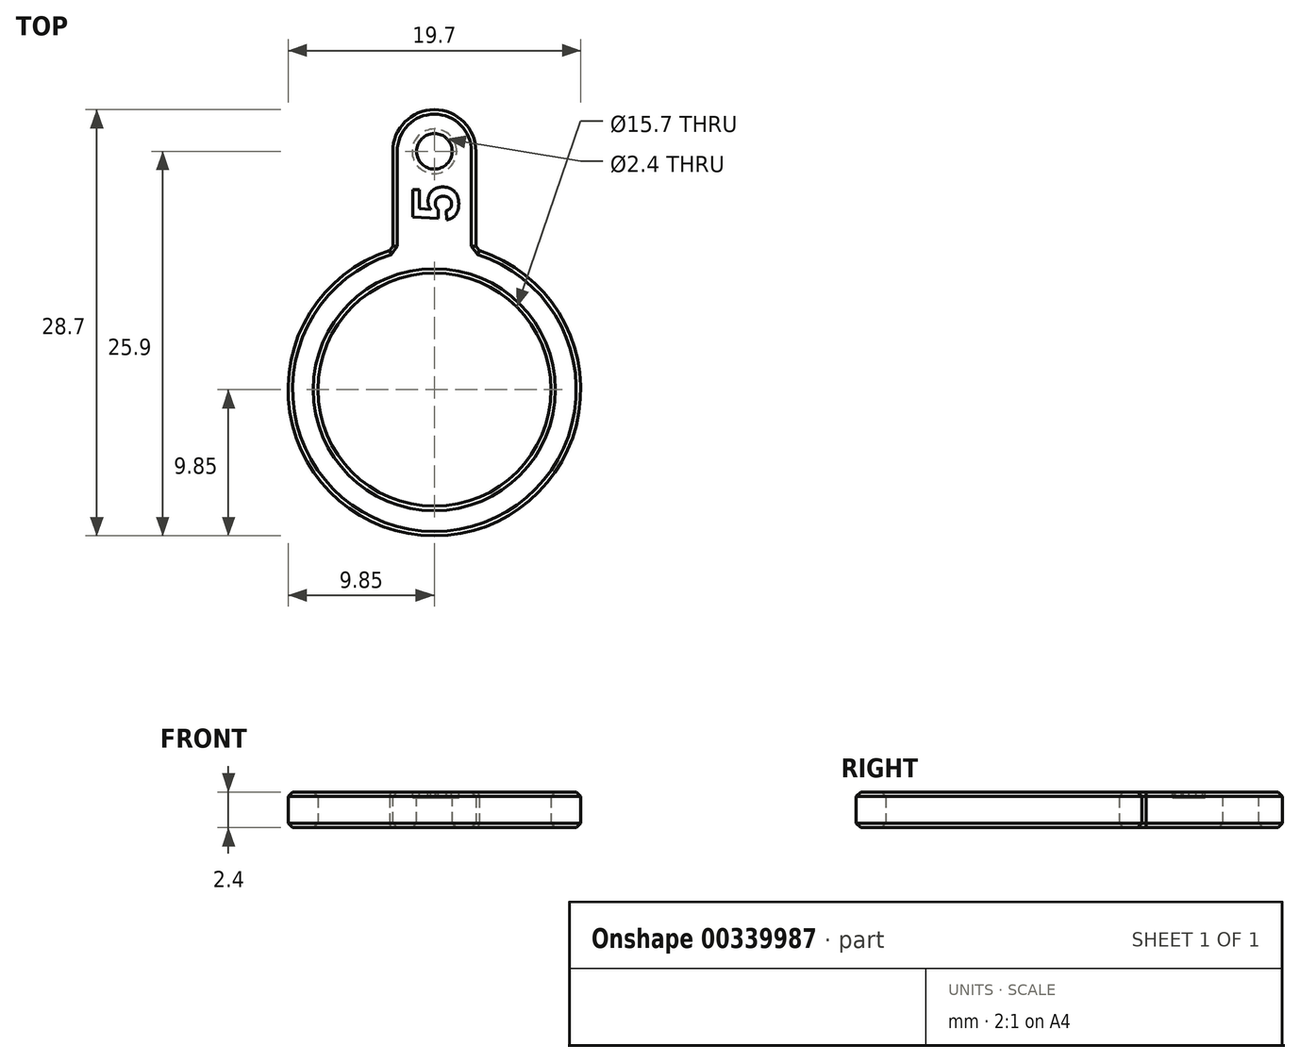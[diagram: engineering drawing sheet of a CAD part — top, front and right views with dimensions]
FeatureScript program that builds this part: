
annotation { "Feature Type Name" : "Feature", "Feature Type Description" : "" }
export const myFeature = defineFeature(function(context is Context, id is Id, definition is map)
    precondition{}
    {
        {
            var Q0;
            Q0=qCreatedBy(makeId("Top.planeOp"),FACE);
            var sketch = newSketch(context, id + "F0", { "sketchPlane" : qUnion([Q0])});
            skCircle(sketch, "E0", {"center": v(0, 0) * mm, "radius": 7.85 * mm});
            skCircle(sketch, "E1", {"center": v(0, 0) * mm, "radius": 9.85 * mm});
            skLineSegment(sketch, "E2.bottom", {"start": v(2.8, 0.85) * mm, "end": v(-2.8, 0.85) * mm});
            skLineSegment(sketch, "E2.top", {"start": v(2.8, 18.85) * mm, "end": v(-2.8, 18.85) * mm});
            skLineSegment(sketch, "E2.left", {"start": v(2.8, 0.85) * mm, "end": v(2.8, 18.85) * mm});
            skLineSegment(sketch, "E2.right", {"start": v(-2.8, 0.85) * mm, "end": v(-2.8, 18.85) * mm});
            skPoint(sketch, "E2.middle", {"position": v(0, 9.85) * mm});
            skSolve(sketch);
        }
        {
            var Q0;
            Q0=qSketchRegion(id+"F0",true);
            extrude(context, id + "F1", {"entities" : qUnion([Q0]), "depth" : 2.4 * mm});
        }
        {
            var Q0;
            Q0=makeQuery(id+"F1.opExtrude","SWEPT_EDGE",EDGE,{"disambiguationData":[OSD([sQuery(id+"F0.wireOp",EDGE,"E2.top"),sQuery(id+"F0.wireOp",EDGE,"E2.right")])]});
            var Q1;
            Q1=makeQuery(id+"F1.opExtrude","SWEPT_EDGE",EDGE,{"disambiguationData":[OSD([sQuery(id+"F0.wireOp",EDGE,"E2.top"),sQuery(id+"F0.wireOp",EDGE,"E2.left")])]});
            fillet(context, id + "F2", {"entities" : qUnion([Q0, Q1]), "radius" : 2.8 * mm, "tangentPropagation" : true, "allowEdgeOverflow" : false});
        }
        {
            var Q0;
            Q0=makeQuery(id+"F1.opExtrude","CAP_FACE",FACE,{"disambiguationData":[OSD([sQuery(id+"F0.wireOp",EDGE,"E0"),sQuery(id+"F0.wireOp",EDGE,"E1"),sQuery(id+"F0.wireOp",EDGE,"E2.top"),sQuery(id+"F0.wireOp",EDGE,"E2.left"),sQuery(id+"F0.wireOp",EDGE,"E2.right")])],"isStart":false});
            var sketch = newSketch(context, id + "F3", { "sketchPlane" : qUnion([Q0])});
            skCircle(sketch, "E3", {"center": v(0, 16.05) * mm, "radius": 1.2 * mm});
            skSolve(sketch);
        }
        {
            var Q0;
            Q0=qSketchRegion(id+"F3",true);
            extrude(context, id + "F4", {"entities" : qUnion([Q0]), "operationType" : NewBodyOperationType.REMOVE, "oppositeDirection" : true, "depth" : 25 * mm});
        }
        {
            var Q0;
            Q0=makeQuery(id+"F4.boolean.opBoolean","COPY",EDGE,{"derivedFrom":makeQuery(id+"F4.opExtrude","CAP_EDGE",EDGE,{"disambiguationData":[OSD([sQuery(id+"F3.wireOp",EDGE,"E3")])],"isStart":true})});
            var Q1;
            Q1=makeQuery(id+"F4.boolean.opBoolean","INTERSECT",EDGE,{"derivedFrom":[makeQuery(id+"F1.opExtrude","CAP_FACE",FACE,{"disambiguationData":[OSD([sQuery(id+"F0.wireOp",EDGE,"E0"),sQuery(id+"F0.wireOp",EDGE,"E1"),sQuery(id+"F0.wireOp",EDGE,"E2.top"),sQuery(id+"F0.wireOp",EDGE,"E2.left"),sQuery(id+"F0.wireOp",EDGE,"E2.right")])],"isStart":true}),makeQuery(id+"F4.opExtrude","SWEPT_FACE",FACE,{"disambiguationData":[OSD([sQuery(id+"F3.wireOp",EDGE,"E3")])]})]});
            var Q2;
            {var subQ0=sQuery(id+"F0.wireOp",EDGE,"E2.right");var subQ1=sQuery(id+"F0.wireOp",EDGE,"E2.top");Q2=makeQuery(id+"F2.opFillet","BLEND_EDGE",EDGE,{"blendedFrom":[makeQuery(id+"F1.opExtrude","SWEPT_EDGE",EDGE,{"disambiguationData":[OSD([subQ1,subQ0])]}),makeQuery(id+"F1.opExtrude","CAP_FACE",FACE,{"disambiguationData":[OSD([sQuery(id+"F0.wireOp",EDGE,"E0"),sQuery(id+"F0.wireOp",EDGE,"E1"),subQ1,sQuery(id+"F0.wireOp",EDGE,"E2.left"),subQ0])],"isStart":true})],"blendedInto":[makeQuery(id+"F1.opExtrude","CAP_FACE",FACE,{"disambiguationData":[OSD([sQuery(id+"F0.wireOp",EDGE,"E0"),sQuery(id+"F0.wireOp",EDGE,"E1"),subQ1,sQuery(id+"F0.wireOp",EDGE,"E2.left"),subQ0])],"isStart":true})]});}
            var Q3;
            {var subQ0=sQuery(id+"F0.wireOp",EDGE,"E2.right");var subQ1=sQuery(id+"F0.wireOp",EDGE,"E2.top");Q3=makeQuery(id+"F2.opFillet","BLEND_EDGE",EDGE,{"blendedFrom":[makeQuery(id+"F1.opExtrude","SWEPT_EDGE",EDGE,{"disambiguationData":[OSD([subQ1,subQ0])]}),makeQuery(id+"F1.opExtrude","CAP_FACE",FACE,{"disambiguationData":[OSD([sQuery(id+"F0.wireOp",EDGE,"E0"),sQuery(id+"F0.wireOp",EDGE,"E1"),subQ1,sQuery(id+"F0.wireOp",EDGE,"E2.left"),subQ0])],"isStart":false})],"blendedInto":[makeQuery(id+"F1.opExtrude","CAP_FACE",FACE,{"disambiguationData":[OSD([sQuery(id+"F0.wireOp",EDGE,"E0"),sQuery(id+"F0.wireOp",EDGE,"E1"),subQ1,sQuery(id+"F0.wireOp",EDGE,"E2.left"),subQ0])],"isStart":false})]});}
            var Q4;
            Q4=makeQuery(id+"F1.opExtrude","CAP_EDGE",EDGE,{"disambiguationData":[OSD([sQuery(id+"F0.wireOp",EDGE,"E1")])],"isStart":false});
            var Q5;
            Q5=makeQuery(id+"F1.opExtrude","CAP_EDGE",EDGE,{"disambiguationData":[OSD([sQuery(id+"F0.wireOp",EDGE,"E1")])],"isStart":true});
            var Q6;
            Q6=makeQuery(id+"F1.opExtrude","SWEPT_EDGE",EDGE,{"disambiguationData":[OSD([sQuery(id+"F0.wireOp",EDGE,"E1"),sQuery(id+"F0.wireOp",EDGE,"E2.left")])]});
            var Q7;
            Q7=makeQuery(id+"F1.opExtrude","SWEPT_EDGE",EDGE,{"disambiguationData":[OSD([sQuery(id+"F0.wireOp",EDGE,"E1"),sQuery(id+"F0.wireOp",EDGE,"E2.right")])]});
            var Q8;
            Q8=makeQuery(id+"F1.opExtrude","CAP_EDGE",EDGE,{"disambiguationData":[OSD([sQuery(id+"F0.wireOp",EDGE,"E0")])],"isStart":true});
            var Q9;
            Q9=makeQuery(id+"F1.opExtrude","CAP_EDGE",EDGE,{"disambiguationData":[OSD([sQuery(id+"F0.wireOp",EDGE,"E0")])],"isStart":false});
            chamfer(context, id + "F5", {"entities" : qUnion([Q0, Q1, Q2, Q3, Q4, Q5, Q6, Q7, Q8, Q9]), "width" : 0.3 * mm, "tangentPropagation" : true});
        }
        {
            var Q0;
            Q0=makeQuery(id+"F1.opExtrude","CAP_FACE",FACE,{"disambiguationData":[OSD([sQuery(id+"F0.wireOp",EDGE,"E0"),sQuery(id+"F0.wireOp",EDGE,"E1"),sQuery(id+"F0.wireOp",EDGE,"E2.top"),sQuery(id+"F0.wireOp",EDGE,"E2.left"),sQuery(id+"F0.wireOp",EDGE,"E2.right")])],"isStart":false});
            var sketch = newSketch(context, id + "F6", { "sketchPlane" : qUnion([Q0])});
            skText(sketch, "E4", { "text": "5", "fontName": "Arimo-Bold.ttf"});
            skLineSegment(sketch, "E5", {"start": v(0, 11.3) * mm, "end": v(0, 0) * mm});
            skPoint(sketch, "E5.endSnap0", {"position": v(0, 11.3) * mm});
            const initialGuessF6  = {"E4": [0.0016, 0.0113, 0, 1, 0.0032]};
            skSetInitialGuess(sketch, initialGuessF6);
            skSolve(sketch);
        }
        {
            var Q0;
            Q0=qSketchRegion(id+"F6",true);
            extrude(context, id + "F7", {"entities" : qUnion([Q0]), "operationType" : NewBodyOperationType.REMOVE, "oppositeDirection" : true, "depth" : 0.4 * mm});
        }
    });
